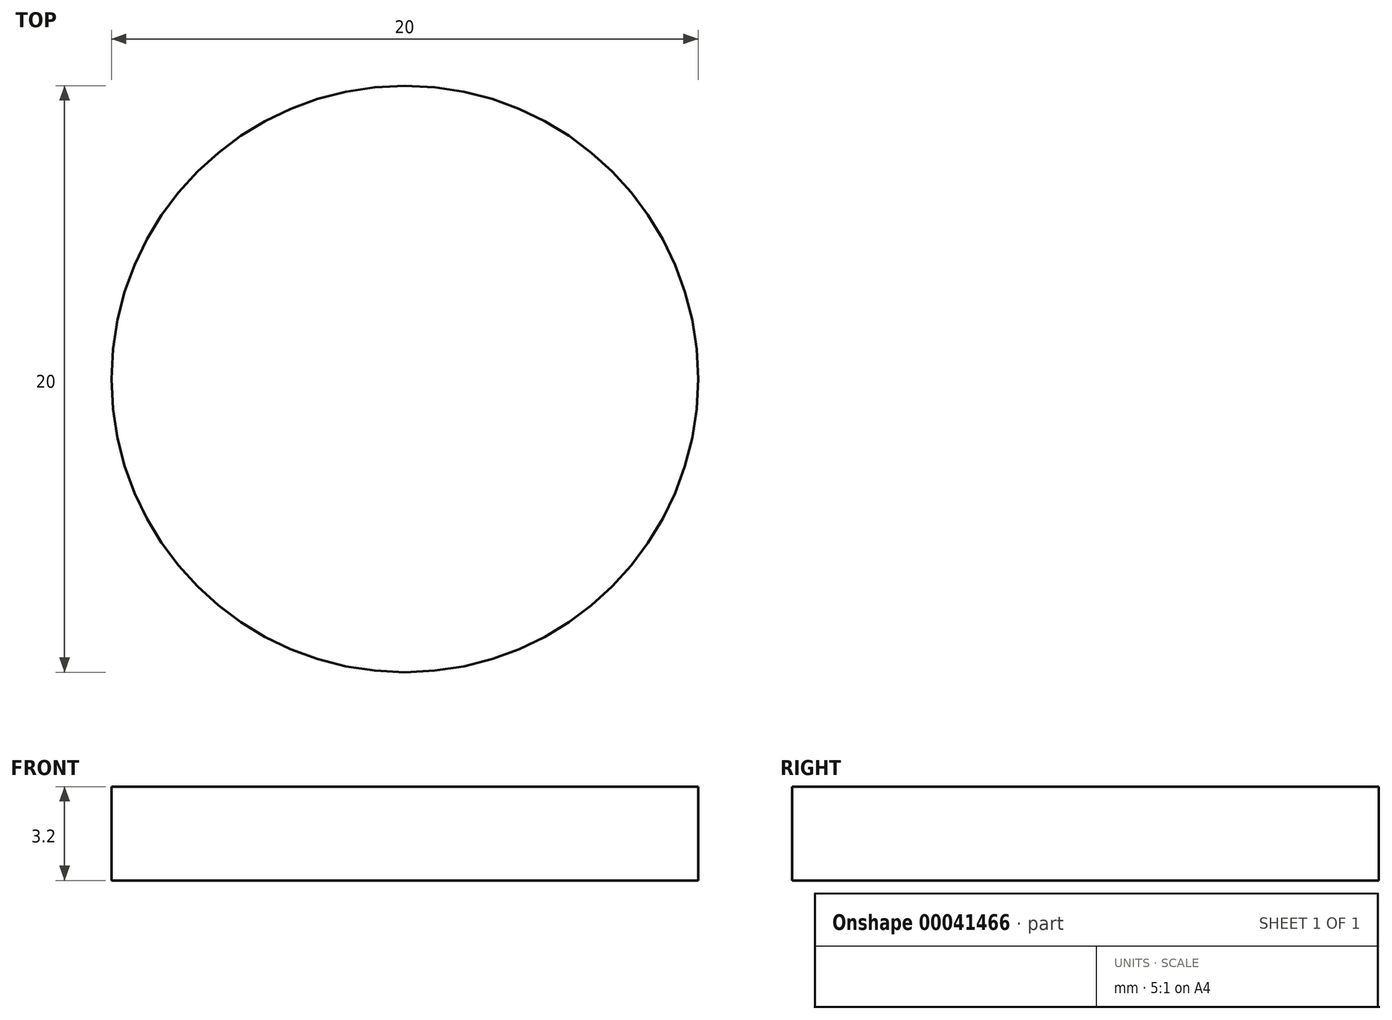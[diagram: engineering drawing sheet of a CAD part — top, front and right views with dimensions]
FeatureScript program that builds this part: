
annotation { "Feature Type Name" : "Feature", "Feature Type Description" : "" }
export const myFeature = defineFeature(function(context is Context, id is Id, definition is map)
    precondition{}
    {
        {
            var Q0;
            Q0=qCreatedBy(makeId("Top.planeOp"),FACE);
            var sketch = newSketch(context, id + "F0", { "sketchPlane" : qUnion([Q0])});
            skCircle(sketch, "E0", {"center": v(0, 0) * mm, "radius": 10 * mm});
            skSolve(sketch);
        }
        {
            var Q0;
            Q0 = qSketchRegion(id + "F0", true);
            extrude(context, id + "F1", {"entities" : qUnion([Q0]), "depth" : 3.2 * mm});
        }
    });
